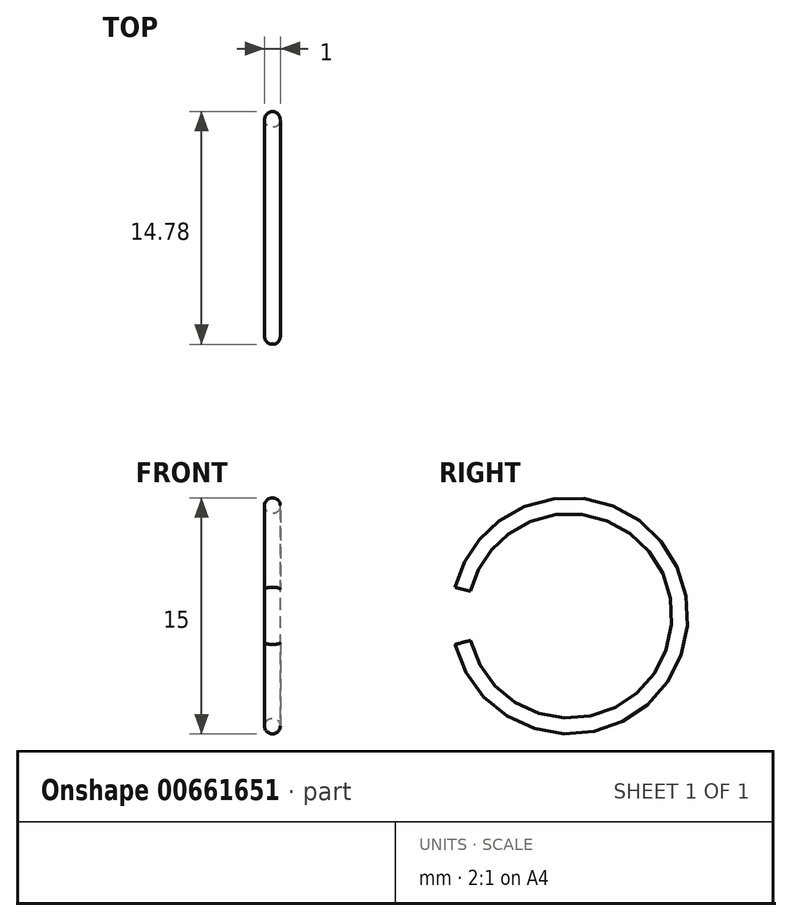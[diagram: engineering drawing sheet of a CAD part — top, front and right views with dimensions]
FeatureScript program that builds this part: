
annotation { "Feature Type Name" : "Feature", "Feature Type Description" : "" }
export const myFeature = defineFeature(function(context is Context, id is Id, definition is map)
    precondition{}
    {
        {
            var Q0;
            Q0=qCreatedBy(makeId("Top.planeOp"),FACE);
            var sketch = newSketch(context, id + "F0", { "sketchPlane" : qUnion([Q0])});
            skLineSegment(sketch, "E0", {"start": v(0, 0) * mm, "end": v(-1.06, 0) * mm, "construction": true});
            skCircle(sketch, "E1", {"center": v(0, 7) * mm, "radius": 0.5 * mm});
            skSolve(sketch);
        }
        {
            var Q0;
            Q0=makeQuery(id+"F0.imprint","IMPRINT",FACE,{"disambiguationData":[TD([[makeQuery(id+"F0.imprint","IMPRINT",EDGE,{"derivedFrom":sQuery(id+"F0.wireOp",EDGE,"E1")}),1.0]])]});
            var Q1;
            Q1=sQuery(id+"F0.wireOp",EDGE,"E0");
            revolve(context, id + "F1", {"entities" : qUnion([Q0]), "axis" : qUnion([Q1]), "revolveType" : RevolveType.SYMMETRIC, "angle" : 332 * degree});
        }
    });
